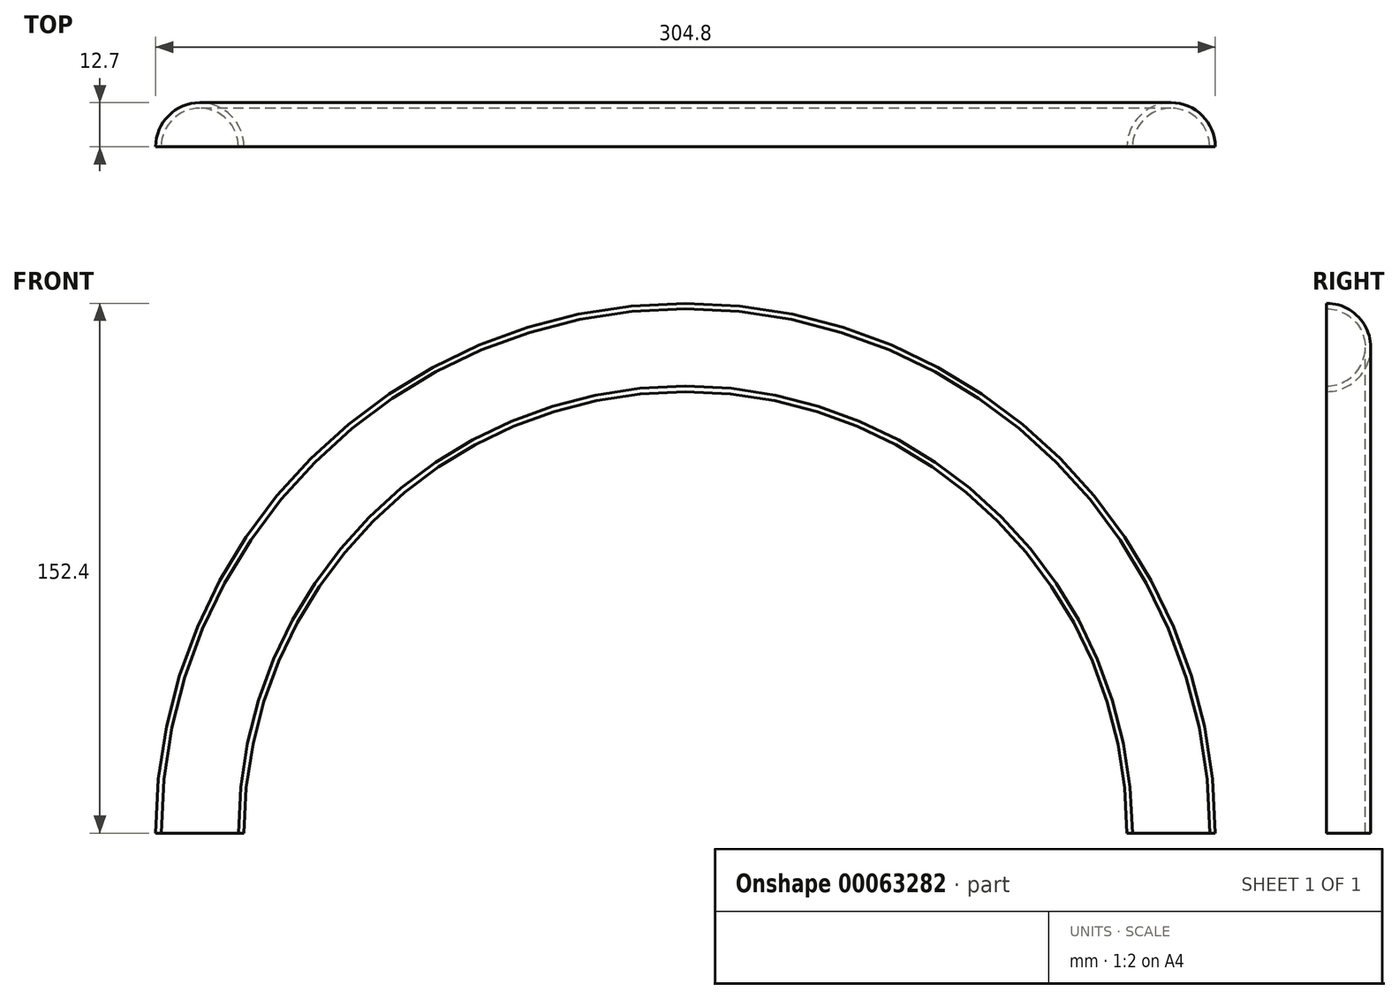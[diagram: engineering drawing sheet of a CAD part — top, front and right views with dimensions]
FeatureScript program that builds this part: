
annotation { "Feature Type Name" : "Feature", "Feature Type Description" : "" }
export const myFeature = defineFeature(function(context is Context, id is Id, definition is map)
    precondition{}
    {
        {
            var Q0;
            Q0=qCreatedBy(makeId("Front.planeOp"),FACE);
            var sketch = newSketch(context, id + "F0", { "sketchPlane" : qUnion([Q0])});
            skArc(sketch, "E0", {"start": v(139.7, 0) * mm, "mid": v(0, 139.7) * mm, "end": v(-139.7, 0) * mm});
            skPoint(sketch, "E1", {"position": v(-139.7, 0) * mm});
            skPoint(sketch, "E2", {"position": v(139.7, 0) * mm});
            skSolve(sketch);
        }
        {
            var Q0;
            Q0=qCreatedBy(makeId("Top.planeOp"),FACE);
            var sketch = newSketch(context, id + "F1", { "sketchPlane" : qUnion([Q0])});
            skPoint(sketch, "E3.0", {"position": v(-139.7, 0) * mm});
            skCircle(sketch, "E4", {"center": v(-139.7, 0) * mm, "radius": 12.7 * mm});
            skSolve(sketch);
        }
        {
            var Q0;
            Q0=qSketchRegion(id+"F1",true);
            var Q1;
            Q1=qConstructionFilter(qBodyType(qCreatedBy(id+"F0",EDGE),BodyType.WIRE),ConstructionObject.NO);
            sweep(context, id + "F2", {"profiles" : qUnion([Q0]), "path" : qUnion([Q1])});
        }
        {
            var Q0;
            Q0=makeQuery(id+"F2.opSweep","CAP_FACE",FACE,{"disambiguationData":[OSD([sQuery(id+"F0.wireOp",VERTEX,"E0.end"),sQuery(id+"F1.wireOp",EDGE,"E4")])],"isStart":true});
            var sketch = newSketch(context, id + "F3", { "sketchPlane" : qUnion([Q0])});
            skLineSegment(sketch, "E5.0", {"start": v(-152.4, 0) * mm, "end": v(-152.4, 0) * mm});
            skArc(sketch, "E6.0.0", {"start": v(-127, 0) * mm, "mid": v(-139.7, 12.7) * mm, "end": v(-152.4, 0) * mm});
            skLineSegment(sketch, "E7", {"start": v(-152.4, 0) * mm, "end": v(-127, 0) * mm});
            skArc(sketch, "E8", {"start": v(-127, 0) * mm, "mid": v(-139.7, 12.4) * mm, "end": v(-152.4, 0) * mm});
            skSolve(sketch);
        }
        {
            var Q0;
            Q0=qSketchRegion(id+"F3",true);
            var Q1;
            Q1=qConstructionFilter(qBodyType(qCreatedBy(id+"F0",EDGE),BodyType.WIRE),ConstructionObject.NO);
            sweep(context, id + "F4", {"operationType" : NewBodyOperationType.REMOVE, "profiles" : qUnion([Q0]), "path" : qUnion([Q1])});
        }
        {
            var Q0;
            Q0=makeQuery(id+"F2.opSweep","CAP_FACE",FACE,{"disambiguationData":[OSD([sQuery(id+"F0.wireOp",VERTEX,"E0.end"),sQuery(id+"F1.wireOp",EDGE,"E4")])],"isStart":true});
            var sketch = newSketch(context, id + "F5", { "sketchPlane" : qUnion([Q0])});
            skLineSegment(sketch, "E9", {"start": v(-152.4, 0) * mm, "end": v(-127, 0) * mm});
            skCircle(sketch, "E10", {"center": v(-139.7, 0) * mm, "radius": 11.11 * mm});
            skSolve(sketch);
        }
        {
            var Q0;
            Q0=qSketchRegion(id+"F5",true);
            var Q1;
            Q1=qConstructionFilter(qBodyType(qCreatedBy(id+"F0",EDGE),BodyType.WIRE),ConstructionObject.NO);
            sweep(context, id + "F6", {"operationType" : NewBodyOperationType.REMOVE, "profiles" : qUnion([Q0]), "path" : qUnion([Q1])});
        }
    });
